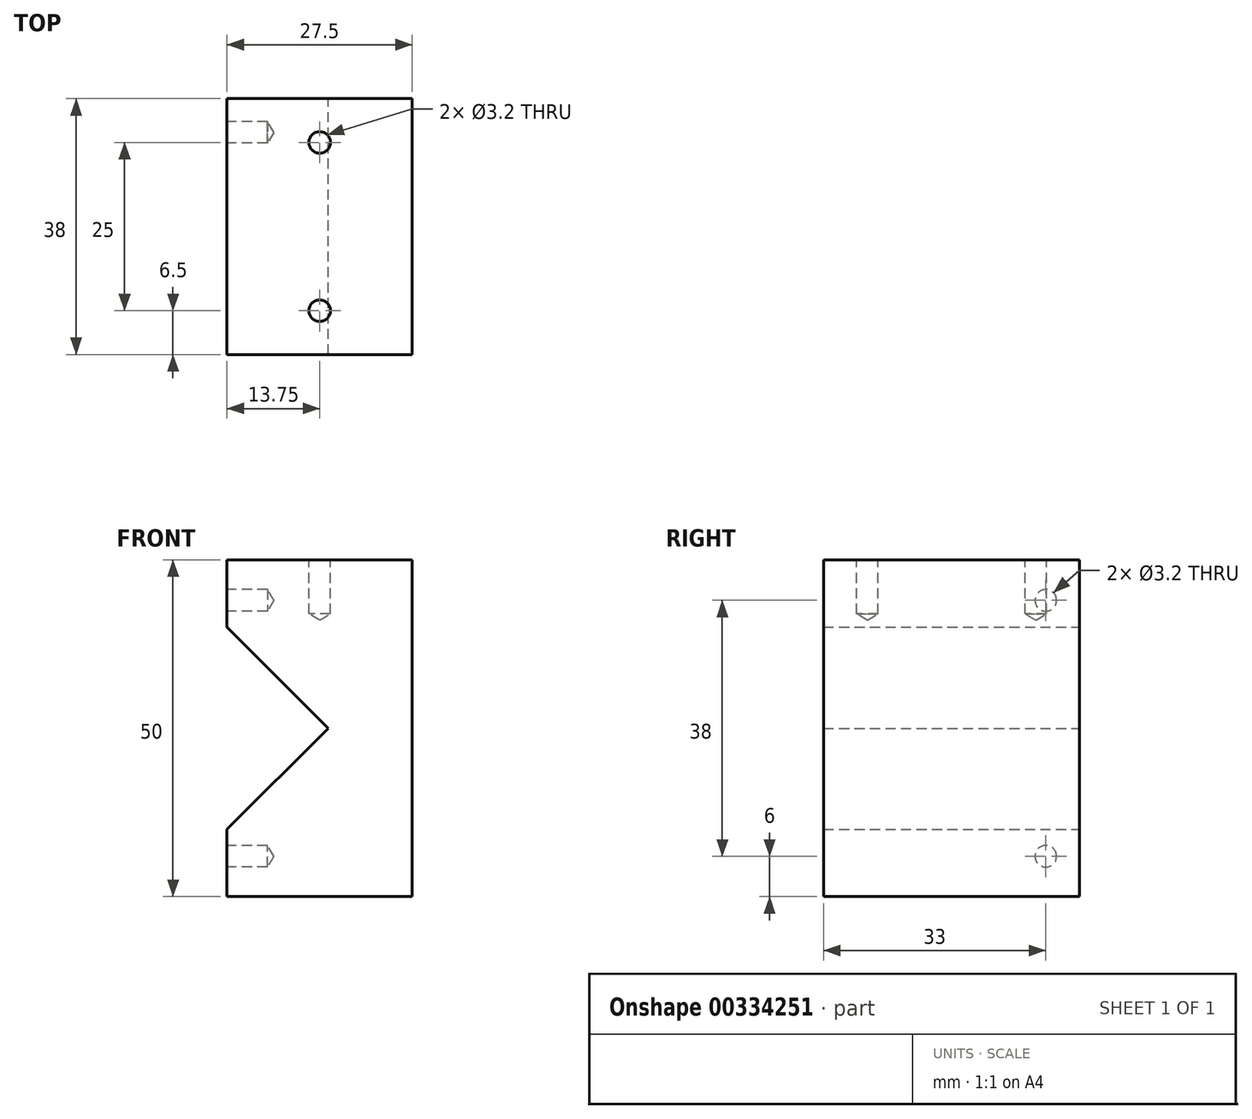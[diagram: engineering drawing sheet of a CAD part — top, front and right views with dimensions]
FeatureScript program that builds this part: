
annotation { "Feature Type Name" : "Feature", "Feature Type Description" : "" }
export const myFeature = defineFeature(function(context is Context, id is Id, definition is map)
    precondition{}
    {
        {
            var Q0;
            Q0=qCreatedBy(makeId("Front.planeOp"),FACE);
            var sketch = newSketch(context, id + "F0", { "sketchPlane" : qUnion([Q0])});
            skLineSegment(sketch, "E0", {"start": v(0, 25) * mm, "end": v(0, 15) * mm});
            skLineSegment(sketch, "E1", {"start": v(0, 15) * mm, "end": v(15, 0) * mm});
            skLineSegment(sketch, "E2", {"start": v(15, 0) * mm, "end": v(27.5, 0) * mm});
            skLineSegment(sketch, "E3", {"start": v(27.5, 0) * mm, "end": v(27.5, 25) * mm});
            skLineSegment(sketch, "E4", {"start": v(27.5, 25) * mm, "end": v(0, 25) * mm});
            skPoint(sketch, "E5", {"position": v(0, 20) * mm});
            skSolve(sketch);
        }
        {
            var Q0;
            Q0=makeQuery(id+"F0.imprint","IMPRINT",FACE,{"disambiguationData":[TD([[makeQuery(id+"F0.imprint","IMPRINT",EDGE,{"derivedFrom":sQuery(id+"F0.wireOp",EDGE,"E0")}),1.0]])]});
            extrude(context, id + "F1", {"entities" : qUnion([Q0]), "endBound" : BoundingType.SYMMETRIC, "depth" : 38 * mm});
        }
        {
            var Q0;
            Q0=makeQuery(id+"F1.opExtrude","SWEPT_FACE",FACE,{"disambiguationData":[OSD([sQuery(id+"F0.wireOp",EDGE,"E0")])]});
            var sketch = newSketch(context, id + "F2", { "sketchPlane" : qUnion([Q0])});
            skPoint(sketch, "E6", {"position": v(-14, 19) * mm});
            skSolve(sketch);
        }
        {
            var Q0;
            Q0=sQuery(id+"F2.wireOp",VERTEX,"E6");
            var Q1;
            Q1=makeQuery(id+"F1.opExtrude","SWEPT_BODY",BODY,{"disambiguationData":[OSD([sQuery(id+"F0.wireOp",EDGE,"E0"),sQuery(id+"F0.wireOp",EDGE,"E1"),sQuery(id+"F0.wireOp",EDGE,"E2"),sQuery(id+"F0.wireOp",EDGE,"E3"),sQuery(id+"F0.wireOp",EDGE,"E4")])]});
            hole(context, id + "F3", {"style" : HoleStyle.SIMPLE, "endStyle" : HoleEndStyle.BLIND, "standardTappedOrClearance" : lookupTablePath({ "standard" : "ISO", "engagement" : "75%", "pitch" : "0.75 mm", "size" : "M4", "type" : "Tapped" }), "standardBlindInLast" : lookupTablePath({ "standard" : "ISO", "engagement" : "75%", "pitch" : "0.75 mm", "size" : "M4", "type" : "Tapped" }), "holeDiameter" : 3.2 * mm, "showTappedDepth" : true, "holeDepth" : 6 * mm, "tappedDepth" : 3.75 * mm, "tapClearance" : 3, "locations" : qUnion([Q0]), "scope" : qUnion([Q1])});
        }
        {
            var Q0;
            Q0=makeQuery(id+"F1.opExtrude","SWEPT_BODY",BODY,{"disambiguationData":[OSD([sQuery(id+"F0.wireOp",EDGE,"E0"),sQuery(id+"F0.wireOp",EDGE,"E1"),sQuery(id+"F0.wireOp",EDGE,"E2"),sQuery(id+"F0.wireOp",EDGE,"E3"),sQuery(id+"F0.wireOp",EDGE,"E4")])]});
            var Q1;
            Q1=qCreatedBy(makeId("Top.planeOp"),FACE);
            mirror(context, id + "F4", {"operationType" : NewBodyOperationType.ADD, "entities" : qUnion([Q0]), "mirrorPlane" : qUnion([Q1])});
        }
        {
            var Q0;
            Q0=makeQuery(id+"F1.opExtrude","SWEPT_FACE",FACE,{"disambiguationData":[OSD([sQuery(id+"F0.wireOp",EDGE,"E4")])]});
            var sketch = newSketch(context, id + "F5", { "sketchPlane" : qUnion([Q0])});
            skPoint(sketch, "E7", {"position": v(13.75, -12.5) * mm});
            skPoint(sketch, "E8", {"position": v(13.75, 12.5) * mm});
            skLineSegment(sketch, "E9", {"start": v(13.75, -19) * mm, "end": v(13.75, 19) * mm, "construction": true});
            skPoint(sketch, "E10", {"position": v(13.75, 0) * mm});
            skSolve(sketch);
        }
        {
            var Q0;
            Q0=sQuery(id+"F5.wireOp",VERTEX,"E7");
            var Q1;
            Q1=sQuery(id+"F5.wireOp",VERTEX,"E8");
            var Q2;
            Q2=makeQuery(id+"F1.opExtrude","SWEPT_BODY",BODY,{"disambiguationData":[OSD([sQuery(id+"F0.wireOp",EDGE,"E0"),sQuery(id+"F0.wireOp",EDGE,"E1"),sQuery(id+"F0.wireOp",EDGE,"E2"),sQuery(id+"F0.wireOp",EDGE,"E3"),sQuery(id+"F0.wireOp",EDGE,"E4")])]});
            hole(context, id + "F6", {"style" : HoleStyle.SIMPLE, "endStyle" : HoleEndStyle.BLIND, "standardTappedOrClearance" : lookupTablePath({ "standard" : "ISO", "engagement" : "75%", "pitch" : "0.75 mm", "size" : "M4", "type" : "Tapped" }), "standardBlindInLast" : lookupTablePath({ "standard" : "ISO", "engagement" : "75%", "pitch" : "0.75 mm", "size" : "M4", "type" : "Tapped" }), "holeDiameter" : 3.2 * mm, "showTappedDepth" : true, "holeDepth" : 8 * mm, "tappedDepth" : 5.75 * mm, "tapClearance" : 3, "locations" : qUnion([Q0, Q1]), "scope" : qUnion([Q2])});
        }
    });
